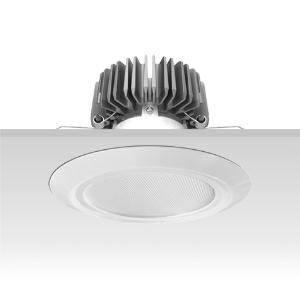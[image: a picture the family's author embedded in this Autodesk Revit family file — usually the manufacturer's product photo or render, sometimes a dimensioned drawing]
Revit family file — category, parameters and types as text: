
# Revit family: 3f_filippi_-_3f_reno_bianco_ampio_3f_filippi_-_30621_a01048_-_3f_reno_200_wh_2000-840_wide___smp_wh_b443
name_source: partatom
category: Lighting Fixtures
units: mm (PartAtom-declared; Revit-internal decimal feet)

## family parameters
Cut with Voids When Loaded = No
Host = Face
Light Source = No
Part Type = Normal
Room Calculation Point = No
Round Connector Dimension = Use Diameter
Shared = No

## types (1)
- 3F Filippi - 3F Reno Bianco Ampio (1 x LED, 1723 lm, 20 W, 4000 K)
    Apparent Load = 20 VA
    Approval mark = CE
    CIE Flux Codes = 74 92 98 100 100
    Color Rendering = 80
    Color Temperature = 4000 K
    Control Gear = Electronic ballast
    Default Elevation = 1800 mm
    Description = ILLUMINOTECHNICAL
Luminous efficiency 100% (DLOR 100%, ULOR 0%).
Initial luminous flux of the luminaire 1723 lm.
Direct symmetric wide distribution.
Installation Interdistance Transv.D = 1.06 x hu - Long.D = 1.04 x hu.
Average luminance <3000 cd/m² for radial angles >65°.
Tabular UGR (CIE 117 - 4H-8H; S=0.25H; 70/50/20): RUG 21.4 - 21.3.
Beam angle: 70° - 69°.
Luminous efficacy 86 lm/W.
Lifetime (L90/B10): 30000 h. (tq+25°C)
Lifetime (L85/B10): 50000 h. (tq+25°C)
Lifetime (L70/B10): 80000 h. (tq+25°C)
Sudden decreased luminous flux after 50000 hours: 0% (C0).
Photobiological safety in compliance with IEC/TR 62778: RG0 risk exempt, (IEC 62471).
In compliance with IEC/EN 62722-2-1 - IEC/EN 62717 standards.

SOURCE
Compact LED module 2000/840.
Energy efficiency class (UE 2019/2020 - UE 2019/2015): D.
CIE 13.3 Colour rendering index: CRI >80 (R9 <50%).
IES TM-30 Fidelity Index: Rf = 84 Rg = 95.
CCT nominal colour temperature 4000 K.
Colour initial tolerance (MacAdam): SDCM 3.
Zhaga Book 3 compliant.

MECHANICAL
Passive heat dissipator in die-casting aluminium, oversized, for optimum thermal management of the LED module.
Parabolic element with graduated/concentric rings in white polycarbonate.
Transparent external lens with glossy and satin differentiated surfaces, with a cooling and anti-insect system in methacrylate (PMMA).
Fastening spring clips in stainless steel.
Dimensions: diameter 226 mm, height 146 mm. Weight 1 kg.
IP44 protection degree for exposed part, IP20 for recessed part.
Mechanical strength to impacts IK05 (0.7 joule).
Glow-wire test resistance 650°C.

ELECTRICAL
Wiring on a separate unit.
Halogen Free electronic wiring 230V-50/60Hz, power factor 0.95, THD <25%, constant output current, SELV, class II, 1 driver.
Power of the luminaire 20 W.
ENEC - CE.
SAFE FLICKER: PstLM=<1 and SVM=<0.4 (IEC TR 61547-1 and IEC TR 63158), to ensure a more comfortable and safe light.
Luminaire compliant with EN 60598-2-22 for power supply from a centralised emergency system CPSS (Central Power Supply System), not incorporated in the luminaire - high risk areas excluded. The default power and flux are 100% in AC and 100% in DC.
Ambient temperature from 0°C to +25°C.
Temperature class T6 max 85°C.
Relative humidity UR: <85%.

INSTALLATION
Pull-up recessed fitting.
False ceiling carving: 200 mm.
All accessories dedicated to this product are available on the Catalog and on our website www.3F-Filippi.com.

ACCESSORIES
A01048 - Anti-glare microprismatic SMP diffuser in methacrylate (PMMA), locked and in line with the trim, in white polycarbonate.

APPLICATIONS
Suitable product for food production plants (HACCP), IFS (Food Version 6), BRC (GSFS Food Version 7).
Environments: architectural, commercial, exhibition areas, transit areas, corridors, shops, display windows, service areas.
In false ceilings with narrow voids.

WARNING
Luminaire designed for disposal/recycling at end-of-life.
Replaceable (LED only) light source by a professional. Replaceable control gear by a professional.
    Height = 0 mm  [stored 0 ft]
    Lamp = 1 x LED
    Lamp Light Flux = 1723 lm
    Lamp Power = 20 W
    Lamp count = 1
    Length = 226 mm
    Lifetime = 50000 h
    Luminous efficacy = 86 lm/W
    Manufacturer = 3F Filippi
    ModVariant = No
    Model = 3F Filippi - 30621+A01048 - 3F Reno 200 WH 2000-840 WIDE + SMP WH
    Mounting Place = Ceiling
    Mounting Type = Recessed
    Number of Poles = 1
    OnlyDefault = Yes
    Power Factor = 1
    Product Name = 3F Filippi - 3F Reno Bianco Ampio
    Product group = recessed luminaire
    ProductGroupID = 4
    Protection Class = Protection class II
    Protection Degree = IP 20
    RLX_Detail_Level = 1
    RLX_Emergency_Light_Flux = 0 lm
    RLX_Emergency_Type = 0
    RLX_Emergency_Type_DB = No
    RlxData = <blob elided: 94753 chars, md5=deb15720>
    Socket = socket
    Standby Power = 0 W
    System Light Flux = 1723 lm
    System Power = 20 W
    Type Comments = Product without accessories
    Type Image = 3ffilippi_3f_reno_200_wh_vs_smp.jpg
    URL = http://relux.com
    VarID = ---
    Voltage = 0 V
    Weight = 0.00 kg
    Width = 0 mm  [stored 0 ft]

note: [stored X ft] marks values corroborated as IEEE doubles in the binary element streams (Revit-internal decimal feet)

## geometry (parser evidence)
native form markers: Blend x4, Sweep x10
no freeform markers — native parametric forms only
